# Revit family: Diverter-Two_Handle-American_Standard-Boulevard-T431740.rfaxxx
name_source: partatom
category: Plumbing Fixtures
units: mm (PartAtom-declared; Revit-internal decimal feet)

## family parameters
Cut with Voids When Loaded = No
Host = Face
OmniClass Number = 23.65.55.14
OmniClass Title = Valves for Liquid Services
Part Type = Normal
Room Calculation Point = No
Round Connector Dimension = Use Diameter
Shared = Yes

## types (1)
- T431740.295
    8888.120 Diverter Tub Spout = No
    Assembly Code = D2020300
    C = 1/2"
    CW Connection = Yes
    CWFU = 3
    Cold Water Connection Diameter = 0"
    Compliance Certifications = ASSE 1016, ASME A112.18.1 & CSA B125.1
    Default Elevation = 48"
    Description = Boulevard Thermostatic Shower Valve Trim Kit with On/Off Volume Control
    Diameter = 7 15/16"
    Finish = Cast Brass-American Standard-002-Polished Chrome
    HW Connection = Yes
    HWFU = 3
    Hot Water Connection Diameter = 0"
    I/O Constraint = 3/4"
    InletOutlet/2 = 1/4"
    Installation Type = Wall Mounted
    Manufacturer = American Standard
    Material = Cast Brass-American Standard-002-Polished Chrome
    Model = T431740.295
    Price = Prices may vary. Please consult Manufacturer Representative for most up-to-date price list.
    Product Documentation Link = https://americanstandard.box.com
    Product Page URL = https://www.americanstandard-us.com
    R520 = 0"
    R520- Rough Valve Body 1/2" NPT Inlets/Outlets (Sold Separately) = No
    R540 = 0"
    R540- Rough Valve Body 3/4" NPT Inlets/Outlets (Sold Separately) = No
    Tempered Water Connection = Yes
    Tempered Water Connection Diameter = 0"
    Trim Distance from Wall (min. 2"- 2 5/8") = 2"
    Trim Distance from Wall Constraint = 2"
    URL = https://www.americanstandard-us.com
    Valve Visibility = No
    Vent Connection = No
    WFU = 4
    Waste Connection = No

## geometry (parser evidence)
native form markers: Sweep x2
no freeform markers — native parametric forms only
